# Revit family: 01653203
name_source: partatom
category: Plumbing Fixtures
revit_build: Autodesk Revit 2016 (Build: 20150220_1215(x64)
units: mm (PartAtom-declared; Revit-internal decimal feet)

## family parameters
Always vertical = Yes
Cut with Voids When Loaded = No
OmniClass Number = 23.45.55.00
OmniClass Title = Sanitary Faucets, Wastes
Part Type = Normal
Room Calculation Point = No
Round Connector Dimension = Use Diameter
Shared = No
Work Plane-Based = No

## types (1)
- 01653203 Bidet faucet
    2D/3D/BIM Files URL = http://static.hansa.com
    Advanced Features = DZR brass;Low lead <0.3;Waterways without nickel coating
    Aerator = Pressure controlled aerator;Ball Joint Aerator;HONEYCOMB®
    Approval ABP = P-IX 28470/IA
    AssetType = Fixed
    BIMObjectName = 01653203
    BodyMaterial = Brass
    Brand = Hansa
    Catalog Drawing URL = http://static.hansa.com
    Category = Health & Care
    Class = Single lever
    CloseOffRating = 0
    Color = Chrome
    Connection Size = G3/8
    ConvergoRefNr = 0087-1803-0024-FI
    Customs Code = 84818011
    DN Size = DN15
    DurationUnit = Year
    EAN Number = 4015474266605
    Extensions = Pop-up waste with draw-rod
    FDV Document URL = http://www.hansa.com
    FaucetMainMaterial = Brass
    Features = Single lever
    Finish = Polished
    FlowCoefficient = 0
    Group = Bidet faucets
    IfcExportAs = IfcValveType
    IfcExportType = FAUCET
    InletConnectionSize = 10 mm  [stored 0.0328084 ft]
    Installation Type = Deck mounted
    Installation and Maintenance = http://static.hansa.com
    Lever Handle = Lever with H+C symbol
    ManufacterURL = http://www.hansa.com
    Manufacturer = Hansa
    ManufacturerName = Hansa
    Material = Brass
    Model = 01653203 Bidet faucet
    ModelReference = 01653203
    Mounting Holes = 1 mounting hole
    NBSDescription = Water supply fittings for wash basins and troughs
    NBSReference = 45-35-70/371
    Name = 01653203 Bidet faucet
    Name_en = 01653203 Bidet faucet
    NominalDepth = 169 mm
    NominalHeight = 139 mm
    NominalWidth = 58 mm
    Package Weight = 1.96 kg
    Package external Dimensions = 606 x 224 x 88
    Pipes = Flexible inlet pipes
    Product Code = 01653203
    Product Datasheet = http://www.hansa.com
    Product Family = HANSAMEDIPRO
    Product Image URL = http://static.hansa.com
    Product URL = http://static.hansa.com
    Revision = 2
    Shape = Sculptured
    Size = 58x169x139 mm
    Spare Parts = http://static.hansa.com
    Spout Type = Fixed spout
    URL ABP = http://static.hansa.com
    Uniclass2 = Pr_40_30_96_96
    Uniclass2015Description = Washbasin manual water supply sets
    Uniclass2015Reference = Pr_40_20_87_96
    Version = 2
    VersionDate = 01/01/2019
    WarrantyDescription = http://warranty.hansa.com
    WarrantyDurationUnit = Year

note: [stored X ft] marks values corroborated as IEEE doubles in the binary element streams (Revit-internal decimal feet)

## geometry (parser evidence)
native form markers: Sweep x4
no freeform markers — native parametric forms only
